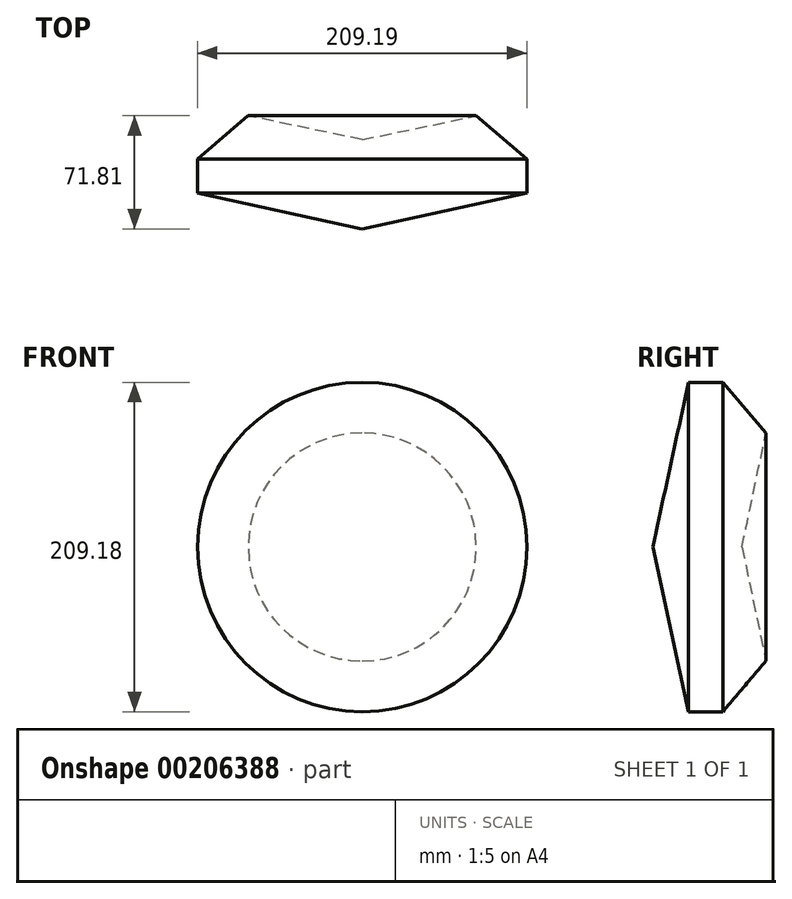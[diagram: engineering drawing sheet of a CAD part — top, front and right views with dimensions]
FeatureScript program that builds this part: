
annotation { "Feature Type Name" : "Feature", "Feature Type Description" : "" }
export const myFeature = defineFeature(function(context is Context, id is Id, definition is map)
    precondition{}
    {
        {
            var Q0;
            Q0=qCreatedBy(makeId("Top.planeOp"),FACE);
            var sketch = newSketch(context, id + "F0", { "sketchPlane" : qUnion([Q0])});
            skLineSegment(sketch, "E0", {"start": v(-47.98, -17.13) * mm, "end": v(-47.98, -38.89) * mm});
            skLineSegment(sketch, "E1", {"start": v(-47.98, -38.89) * mm, "end": v(56.62, -61.53) * mm});
            skLineSegment(sketch, "E2", {"start": v(56.62, -61.53) * mm, "end": v(56.62, -4.92) * mm});
            skLineSegment(sketch, "E3", {"start": v(56.62, -4.92) * mm, "end": v(-15.8, 10.28) * mm});
            skLineSegment(sketch, "E4", {"start": v(-15.8, 10.28) * mm, "end": v(-47.98, -17.13) * mm});
            skSolve(sketch);
        }
        {
            var Q0;
            Q0=makeQuery(id+"F0.imprint","IMPRINT",FACE,{"disambiguationData":[TD([[makeQuery(id+"F0.imprint","IMPRINT",EDGE,{"derivedFrom":sQuery(id+"F0.wireOp",EDGE,"E0")}),1.0]])]});
            var Q1;
            Q1=sQuery(id+"F0.wireOp",EDGE,"E2");
            revolve(context, id + "F1", {"entities" : qUnion([Q0]), "axis" : qUnion([Q1]), "revolveType" : RevolveType.FULL});
        }
    });
